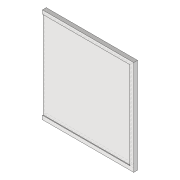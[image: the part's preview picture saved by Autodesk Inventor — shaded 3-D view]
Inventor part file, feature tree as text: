
AUTODESK INVENTOR PART (.ipt)
format: ipt  version: 2020 (Build 240168000, 168)  size: 94,720 bytes
history: native  units: mm
features: extrude x2, sketch x2
ambient origin geometry x8: Origin, YZ Plane, XZ Plane, XY Plane, X Axis, Y Axis, Z Axis, Center Point
bodies: Volumenkörper1 (feature_tree)
feature tree (4):
  extrude  "Extrusion1"  Depth=230.0mm
  extrude  "Extrusion2"  Depth=10.0mm
  sketch  "Skizze1"  dims[d0=230.0mm d1=230.0mm]
  sketch  "Skizze2"  dims[d2=3.0mm d3=0.0mm d4=10.0mm d5=10.0mm d6=10.0mm d7=10.0mm d8=0.0mm]
